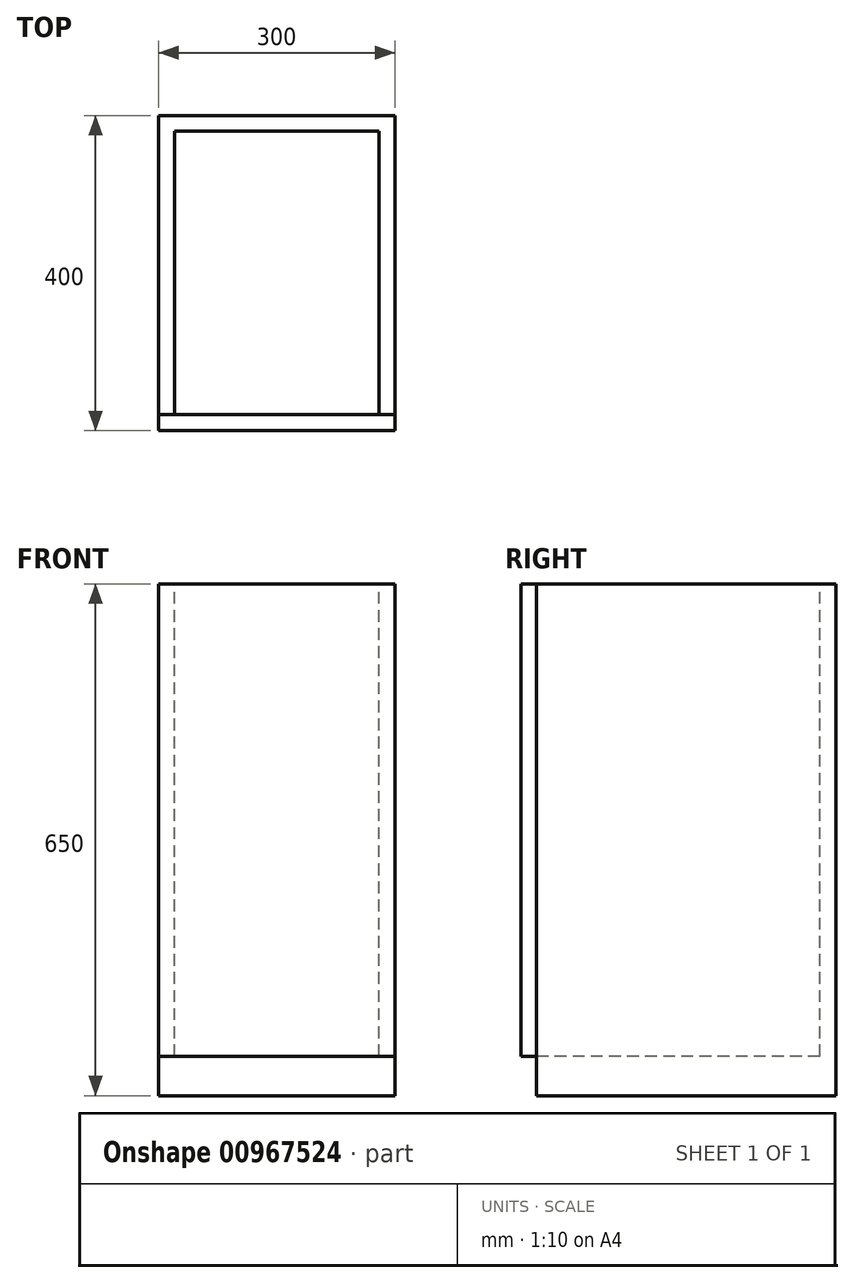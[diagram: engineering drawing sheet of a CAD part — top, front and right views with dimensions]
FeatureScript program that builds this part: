
annotation { "Feature Type Name" : "Feature", "Feature Type Description" : "" }
export const myFeature = defineFeature(function(context is Context, id is Id, definition is map)
    precondition{}
    {
        {
            assignVariable(context, id + "F0", {"variableType" : VariableType.LENGTH, "name" : "H", "lengthValue" : 700 * mm});
        }
        {
            assignVariable(context, id + "F1", {"variableType" : VariableType.LENGTH, "name" : "h", "lengthValue" : 50 * mm});
        }
        {
            var Q0;
            Q0=qCreatedBy(makeId("Top.planeOp"),FACE);
            var sketch = newSketch(context, id + "F2", { "sketchPlane" : qUnion([Q0])});
            skLineSegment(sketch, "E0.bottom", {"start": v(0, 0) * mm, "end": v(300, 0) * mm});
            skLineSegment(sketch, "E0.top", {"start": v(0, 380) * mm, "end": v(300, 380) * mm});
            skLineSegment(sketch, "E0.left", {"start": v(0, 0) * mm, "end": v(0, 380) * mm});
            skLineSegment(sketch, "E0.right", {"start": v(300, 0) * mm, "end": v(300, 380) * mm});
            skSolve(sketch);
        }
        {
            var Q0;
            Q0 = qSketchRegion(id + "F2", true);
            extrude(context, id + "F3", {"entities" : qUnion([Q0]), "depth" : getVariable(context, 'H') - 50 * mm, "offsetDistance" : 25 * mm});
        }
        {
            var Q0;
            Q0=makeQuery(id+"F3.opExtrude","SWEPT_FACE",FACE,{"disambiguationData":[OSD([sQuery(id+"F2.wireOp",EDGE,"E0.bottom")])]});
            var sketch = newSketch(context, id + "F4", { "sketchPlane" : qUnion([Q0])});
            skLineSegment(sketch, "E1.bottom", {"start": v(0, 650) * mm, "end": v(300, 650) * mm});
            skLineSegment(sketch, "E1.top", {"start": v(0, 50) * mm, "end": v(300, 50) * mm});
            skLineSegment(sketch, "E1.left", {"start": v(0, 650) * mm, "end": v(0, 50) * mm});
            skLineSegment(sketch, "E1.right", {"start": v(300, 650) * mm, "end": v(300, 50) * mm});
            skSolve(sketch);
        }
        {
            var Q0;
            Q0 = qSketchRegion(id + "F4", true);
            extrude(context, id + "F5", {"entities" : qUnion([Q0]), "depth" : 20 * mm, "offsetDistance" : 25 * mm});
        }
        {
            var Q0;
            Q0=makeQuery(id+"F3.opExtrude","CAP_FACE",FACE,{"disambiguationData":[OSD([sQuery(id+"F2.wireOp",EDGE,"E0.bottom"),sQuery(id+"F2.wireOp",EDGE,"E0.top"),sQuery(id+"F2.wireOp",EDGE,"E0.left"),sQuery(id+"F2.wireOp",EDGE,"E0.right")])],"isStart":false});
            var sketch = newSketch(context, id + "F6", { "sketchPlane" : qUnion([Q0])});
            skLineSegment(sketch, "E2.0.0", {"start": v(0, 380) * mm, "end": v(0, 0) * mm, "construction": true});
            skLineSegment(sketch, "E2.0.1", {"start": v(0, 0) * mm, "end": v(300, 0) * mm, "construction": true});
            skLineSegment(sketch, "E2.0.2", {"start": v(300, 0) * mm, "end": v(300, 380) * mm, "construction": true});
            skLineSegment(sketch, "E2.0.3", {"start": v(300, 380) * mm, "end": v(0, 380) * mm, "construction": true});
            skLineSegment(sketch, "E3.0", {"start": v(20, 360) * mm, "end": v(20, 0) * mm});
            skLineSegment(sketch, "E3.1", {"start": v(280, 360) * mm, "end": v(20, 360) * mm});
            skLineSegment(sketch, "E3.2", {"start": v(280, 0) * mm, "end": v(280, 360) * mm});
            skLineSegment(sketch, "E4", {"start": v(20, 0) * mm, "end": v(280, 0) * mm});
            skSolve(sketch);
        }
        {
            var Q0;
            Q0 = qSketchRegion(id + "F6", true);
            extrude(context, id + "F7", {"entities" : qUnion([Q0]), "operationType" : NewBodyOperationType.REMOVE, "endBound" : BoundingType.UP_TO_NEXT, "oppositeDirection" : true, "depth" : 25 * mm, "hasOffset" : true, "offsetDistance" : getVariable(context, 'h')});
        }
    });
